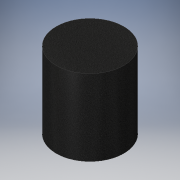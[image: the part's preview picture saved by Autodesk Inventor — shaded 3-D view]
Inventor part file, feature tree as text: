
AUTODESK INVENTOR PART (.ipt)
format: ipt  version: 2019.3 (Build 233278000, 278)  size: 105,984 bytes
history: native  units: mm
features: other x1, extrude x1, sketch x1
ambient origin geometry x8: Origin, YZ Plane, XZ Plane, XY Plane, X Axis, Y Axis, Z Axis, Center Point
bodies: Body1 (feature_tree)
feature tree (3):
  other  "ソリッド1"
  extrude  "押し出し1"  Depth=133.0mm
  sketch  "スケッチ1"
